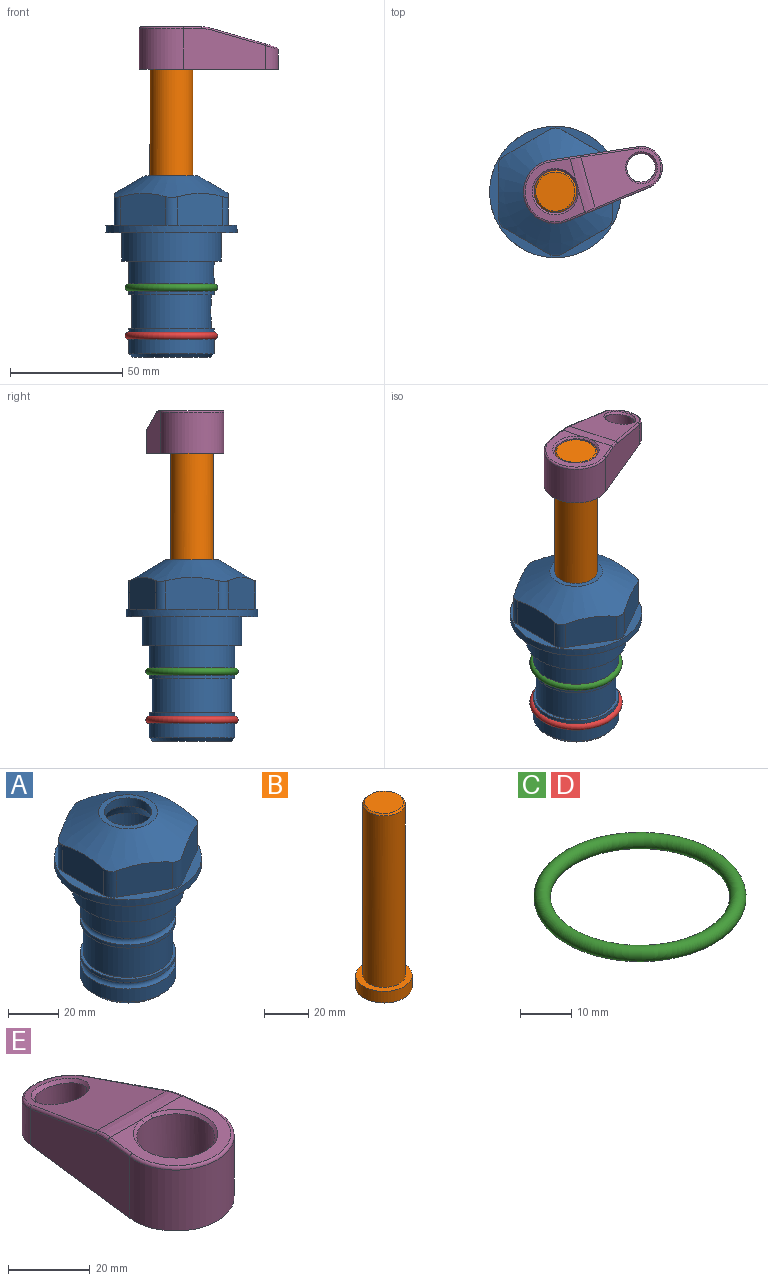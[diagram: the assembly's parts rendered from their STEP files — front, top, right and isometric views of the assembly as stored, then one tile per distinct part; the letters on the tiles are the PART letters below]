
ASSEMBLY  parts=5 mates=4
PART A: 36 faces, bbox 58.7x58.7x81 mm
  f0: cylinder r=17.78mm len=35.56mm, axis (0,0,1), area 1670.8mm2, adj f23,f24,f31
  f1: cylinder r=19.05mm len=38.1mm, axis (0,0,1), area 1191.9mm2, adj f26,f27,f30
  f2: plane 58.66x58.66mm, normal (0,0,-1), area 1150.6mm2, adj f3,f28
  f3: cylinder r=29.33mm len=58.66mm, axis (0,0,-1), area 585.1mm2, adj f2,f4
  f4: plane 58.66x58.66mm, normal (0,0,1), area 475.9mm2, adj f3,f5,f6,f7,f8,f9,f10,f11
  f5: plane 20.32x14.34mm, normal (-0.5,0.87,0), area 324.4mm2, adj f4,f15,f16,f17
  f6: plane 20.32x14.34mm, normal (0.5,0.87,0), area 324.4mm2, adj f4,f14,f15,f17
  f7: plane 23.48x14.34mm, normal (1,0,0), area 324.4mm2, adj f4,f13,f14,f17
  f8: plane 20.32x14.34mm, normal (0.5,-0.87,0), area 324.4mm2, adj f4,f12,f13,f17
  f9: plane 20.32x14.34mm, normal (-0.5,-0.87,0), area 324.4mm2, adj f4,f11,f12,f17
  f10: plane 23.48x14.34mm, normal (-1,0,0), area 324.4mm2, adj f4,f11,f16,f17
  f11: cylinder r=5.08mm len=12.85mm, axis (0,0,-1), area 67.2mm2, adj f4,f9,f10,f17
  f12: cylinder r=5.08mm len=12.85mm, axis (0,0,-1), area 67.2mm2, adj f4,f8,f9,f17
  f13: cylinder r=5.08mm len=12.85mm, axis (0,0,-1), area 67.2mm2, adj f4,f7,f8,f17
  f14: cylinder r=5.08mm len=12.85mm, axis (0,0,-1), area 67.2mm2, adj f4,f6,f7,f17
  f15: cylinder r=5.08mm len=12.85mm, axis (0,0,-1), area 67.2mm2, adj f4,f5,f6,f17
  f16: cylinder r=5.08mm len=12.85mm, axis (0,0,-1), area 67.2mm2, adj f4,f5,f10,f17
  f17: cone r=11.73mm half-angle=60deg, axis (0,0,-1), area 2071.8mm2, adj f5,f6,f7,f8,f9,f10,f11,f12
  f18: plane 23.46x23.46mm, normal (0,0,1), area 147.4mm2, adj f17,f35
  f19: plane 34.93x34.93mm, normal (0,0,-1), area 958mm2, adj f29
  f20: cylinder r=19.05mm len=38.1mm, axis (0,0,1), area 760.1mm2, adj f21,f29
  f21: torus R=19.05mm, axis (0,0,1), area 565.3mm2, adj f20,f22
  f22: cylinder r=19.05mm len=38.1mm, axis (0,0,1), area 190mm2, adj f21,f23
  f23: plane 38.1x38.1mm, normal (0,0,1), area 146.9mm2, adj f0,f22
  f24: plane 38.1x38.1mm, normal (0,0,-1), area 146.9mm2, adj f0,f25
  f25: cylinder r=19.05mm len=38.1mm, axis (0,0,1), area 190mm2, adj f24,f26
  f26: torus R=19.05mm, axis (0,0,1), area 565.3mm2, adj f1,f25
  f27: plane 44.45x44.45mm, normal (0,0,-1), area 411.7mm2, adj f1,f28
  f28: cylinder r=22.23mm len=44.45mm, axis (0,0,1), area 1773.5mm2, adj f2,f27
  f29: cone r=19.05mm half-angle=45deg, axis (0,0,1), area 257.5mm2, adj f19,f20
  f30: cylinder r=3.17mm len=6.75mm, axis (-1,0,0), area 128mm2, adj f1,f33
  f31: cylinder r=3.17mm len=6.35mm, axis (-1,0,0), area 102.5mm2, adj f0,f33
  f32: plane 25.4x25.4mm, normal (0,0,1), area 506.7mm2, adj f33
  f33: cylinder r=12.7mm len=66.42mm, axis (0,0,-1), area 5236.2mm2, adj f30,f31,f32,f34
  f34: cone r=9.53mm half-angle=30deg, axis (0,0,-1), area 443.4mm2, adj f33,f35
  f35: cylinder r=9.53mm len=19.05mm, axis (0,0,-1), area 240.9mm2, adj f18,f34
PART B: 6 faces, bbox 25.4x25.4x101.6 mm
  f0: plane 17.46x17.46mm, normal (0,0,1), area 239.5mm2, adj f5
  f1: plane 25.4x25.4mm, normal (0,0,-1), area 506.7mm2, adj f2
  f2: cylinder r=12.7mm len=25.4mm, axis (0,0,1), area 506.7mm2, adj f1,f3
  f3: plane 25.4x25.4mm, normal (0,0,1), area 221.7mm2, adj f2,f4
  f4: cylinder r=9.53mm len=94.46mm, axis (0,0,1), area 5653mm2, adj f3,f5
  f5: cone r=8.73mm half-angle=45deg, axis (0,0,-1), area 64.4mm2, adj f0,f4
PART C: 1 faces, bbox 44.7x44.7x3.2 mm
  f0: torus R=19.05mm, axis (0,0,1), area 1193.9mm2
PART D: same geometry as C
PART E: 31 faces, bbox 31.7x65.5x19.8 mm
  f0: plane 39.12x18.26mm, normal (0.99,0.12,0), area 612.2mm2, adj f1,f4,f7,f11,f13,f15
  f1: cylinder r=9.53mm len=18.91mm, axis (0,0,-1), area 296.1mm2, adj f0,f2,f7,f17
  f2: plane 39.12x18.26mm, normal (-0.99,0.12,0), area 612.2mm2, adj f1,f4,f7,f12,f14,f16
  f3: cylinder r=6.35mm len=12.7mm, axis (0,0,-1), area 362.4mm2, adj f7,f18
  f4: cylinder r=14.29mm len=28.58mm, axis (0,0,-1), area 882.2mm2, adj f0,f2,f7,f10
  f5: cylinder r=9.53mm len=19.05mm, axis (0,0,-1), area 1092.6mm2, adj f7,f19,f20
  f6: plane 26.99x23.69mm, normal (0,0,1), area 216.2mm2, adj f9,f10,f11,f12,f19
  f7: plane 63.5x28.58mm, normal (0,0,-1), area 661.8mm2, adj f0,f1,f2,f3,f4,f5,f22,f23
  f8: plane 33.52x23.6mm, normal (0,0.26,0.97), area 486mm2, adj f9,f15,f16,f17,f18
  f9: cylinder r=19.05mm len=24.72mm, axis (1,0,0), area 120.4mm2, adj f6,f8,f13,f14,f20
  f10: torus R=13.49mm, axis (0,0,1), area 59mm2, adj f4,f6,f11,f12
  f11: cylinder r=0.79mm len=8.67mm, axis (0.12,-0.99,0), area 10.8mm2, adj f0,f6,f10,f13
  f12: cylinder r=0.79mm len=8.67mm, axis (0.12,0.99,0), area 10.8mm2, adj f2,f6,f10,f14
  f13: bspline ~4.95x1.42mm, area 6.1mm2, adj f0,f9,f11,f15
  f14: bspline ~4.95x1.42mm, area 6.1mm2, adj f2,f9,f12,f16
  f15: cylinder r=0.79mm len=25.95mm, axis (0.12,-0.96,0.26), area 32.9mm2, adj f0,f8,f13,f17
  f16: cylinder r=0.79mm len=25.95mm, axis (0.12,0.96,-0.26), area 32.9mm2, adj f2,f8,f14,f17
  f17: bspline ~18.91x8.38mm, area 30mm2, adj f1,f8,f15,f16
  f18: bspline ~14.29x14.29mm, area 48.3mm2, adj f3,f8
  f19: cone r=9.53mm half-angle=45deg, axis (0,0,1), area 66.5mm2, adj f5,f6,f20
  f20: bspline ~3.22x0.96mm, area 3.5mm2, adj f5,f9,f19
  f21: plane 2.75x2.72mm, normal (0,0,-1), area 2.9mm2, adj f23,f25,f28
  f22: plane 23.05x15.88mm, normal (-0.99,-0.12,0), area 323.6mm2, adj f7,f25,f26,f27,f28,f29
  f23: plane 23.05x15.88mm, normal (0.99,-0.12,0), area 323.6mm2, adj f7,f21,f25,f27,f28,f30
  f24: cylinder r=9.53mm len=10.69mm, axis (0,0,-1), area 114.7mm2, adj f7,f27,f29,f30
  f25: cylinder r=12.7mm len=20.59mm, axis (0,0,-1), area 381.1mm2, adj f7,f21,f22,f23,f26,f28
  f26: plane 2.75x2.72mm, normal (0,0,-1), area 2.9mm2, adj f22,f25,f28
  f27: plane 19.72x18.37mm, normal (0,-0.26,-0.97), area 291.8mm2, adj f22,f23,f24,f28,f29,f30
  f28: cylinder r=15.88mm len=19.92mm, axis (1,0,0), area 54.8mm2, adj f21,f22,f23,f25,f26,f27
  f29: cylinder r=1.59mm len=11mm, axis (0,0,-1), area 34.7mm2, adj f7,f22,f24,f27
  f30: cylinder r=1.59mm len=11mm, axis (0,0,-1), area 34.7mm2, adj f7,f23,f24,f27
PLACE A at identity fixed
PLACE B rot(axis=(0,0,-1),74.4deg) t=(0,0,27.55)mm
PLACE C at identity
PLACE D t=(0,0,-21.59)mm
PLACE E rot(axis=(0,0,-1),74.4deg) t=(0,0,28.35)mm
MATE fastened C.f0 <-> A.f0  axis (0,0,1) through (0,0,-24.51)mm
MATE cylindrical A.f0 <-> B.f2  axis (0,0,1) through (0,0,-50.55)mm
MATE fastened B.f2 <-> E.f4  axis (0,0,1) through (0,0,91.05)mm
MATE fastened D.f0 <-> A.f0  axis (0,0,1) through (0,0,-46.1)mm
